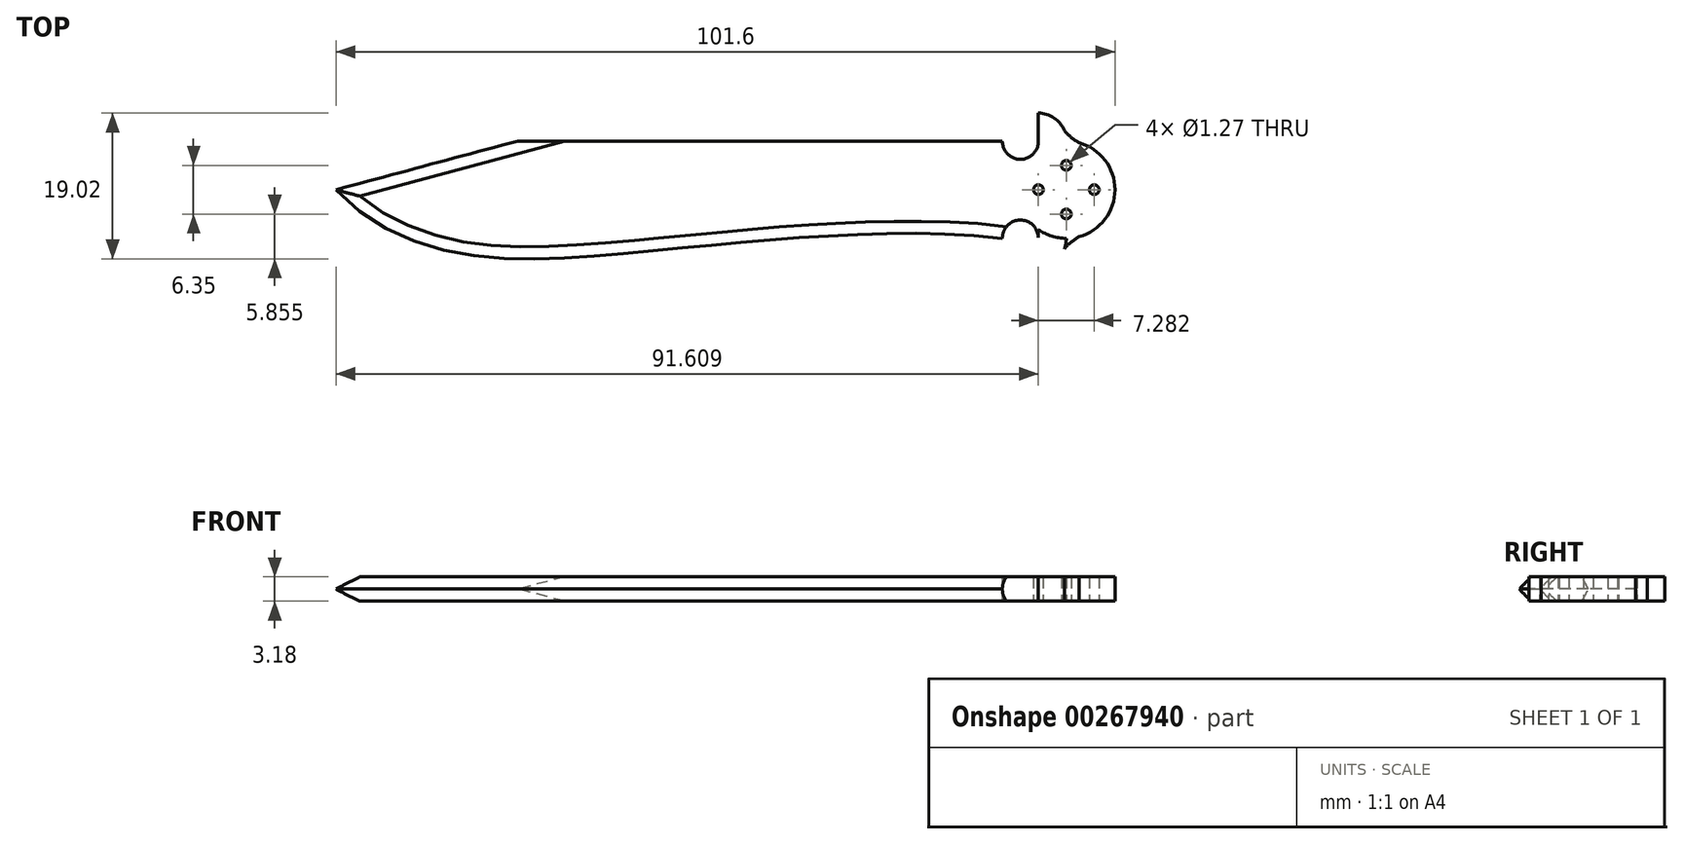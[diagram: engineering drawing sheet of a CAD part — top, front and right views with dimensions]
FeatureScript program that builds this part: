
annotation { "Feature Type Name" : "Feature", "Feature Type Description" : "" }
export const myFeature = defineFeature(function(context is Context, id is Id, definition is map)
    precondition{}
    {
        {
            var Q0;
            Q0=qCreatedBy(makeId("Top.planeOp"),FACE);
            var sketch = newSketch(context, id + "F0", { "sketchPlane" : qUnion([Q0])});
            skCircle(sketch, "E0", {"center": v(0, 0) * mm, "radius": 6.35 * mm});
            skLineSegment(sketch, "E1", {"start": v(0, -6.35) * mm, "end": v(0, 6.35) * mm});
            skArc(sketch, "E2", {"start": v(0, 6.35) * mm, "mid": v(-1.07, 8.92) * mm, "end": v(-3.64, 10) * mm});
            skLineSegment(sketch, "E3", {"start": v(-95.25, 0) * mm, "end": v(6.35, 0) * mm, "construction": true});
            skArc(sketch, "E4.MirrorCS", {"start": v(0, -6.35) * mm, "mid": v(-1.07, -8.92) * mm, "end": v(-3.64, -10) * mm});
            skLineSegment(sketch, "E5", {"start": v(-3.64, 10) * mm, "end": v(-3.64, 5.2) * mm});
            skLineSegment(sketch, "E6", {"start": v(-3.64, -10) * mm, "end": v(-3.64, -5.2) * mm});
            skArc(sketch, "E7", {"start": v(-8.34, 6.35) * mm, "mid": v(-5.99, 3.96) * mm, "end": v(-3.64, 6.35) * mm});
            skArc(sketch, "E8.MirrorCS", {"start": v(-8.34, -6.35) * mm, "mid": v(-5.99, -3.96) * mm, "end": v(-3.64, -6.35) * mm});
            skLineSegment(sketch, "E9", {"start": v(-95.25, 0) * mm, "end": v(-71.55, 6.35) * mm});
            skLineSegment(sketch, "E10", {"start": v(-8.34, 6.35) * mm, "end": v(-71.55, 6.35) * mm});
            skFitSpline(sketch, "E11", {"points": [v(-95.25, 0) * mm, v(-80.99, -7.93) * mm, v(-57.19, -8.28) * mm, v(-8.34, -6.35) * mm], "startDerivative": vector(42.5, -47.89) * mm, "endDerivative": vector(100.7, -12.48) * mm});
            skLineSegment(sketch, "E12", {"start": v(-95.25, 0) * mm, "end": v(-59.24, 6.35) * mm, "construction": true});
            skLineSegment(sketch, "E13", {"start": v(-3.64, 5.2) * mm, "end": v(-3.64, 0) * mm, "construction": true});
            skLineSegment(sketch, "E14", {"start": v(-3.64, 0) * mm, "end": v(-3.64, -5.2) * mm, "construction": true});
            skLineSegment(sketch, "E15.MirrorCS", {"start": v(3.64, 5.2) * mm, "end": v(3.64, 0) * mm, "construction": true});
            skLineSegment(sketch, "E16.MirrorCS", {"start": v(3.64, 0) * mm, "end": v(3.64, -5.2) * mm, "construction": true});
            skCircle(sketch, "E17", {"center": v(-3.64, 0) * mm, "radius": 0.64 * mm});
            skCircle(sketch, "E18", {"center": v(3.64, 0) * mm, "radius": 0.64 * mm});
            skLineSegment(sketch, "E19", {"start": v(0, 0) * mm, "end": v(0, 6.35) * mm, "construction": true});
            skLineSegment(sketch, "E20", {"start": v(0, 0) * mm, "end": v(0, -6.35) * mm, "construction": true});
            skCircle(sketch, "E21", {"center": v(0, -3.17) * mm, "radius": 0.64 * mm});
            skCircle(sketch, "E22", {"center": v(0, 3.17) * mm, "radius": 0.64 * mm});
            skFitSpline(sketch, "E23", {"points": [v(-1.07, 8.92) * mm, v(3.64, 5.2) * mm], "startDerivative": vector(3.04, -6.1) * mm, "endDerivative": vector(5.07, -1.86) * mm});
            skFitSpline(sketch, "E24.MirrorCS", {"points": [v(-1.07, -8.92) * mm, v(3.64, -5.2) * mm], "startDerivative": vector(3.04, 6.1) * mm, "endDerivative": vector(5.07, 1.86) * mm});
            skSolve(sketch);
        }
        {
            var Q0;
            {var subQ0=sQuery(id+"F0.wireOp",EDGE,"E9");Q0=makeQuery(id+"F0.imprint","IMPRINT",FACE,{"disambiguationData":[TD([[makeQuery(id+"F0.imprint","IMPRINT",EDGE,{"derivedFrom":subQ0}),-1.0]])]});}
            var Q1;
            Q1=makeQuery(id+"F0.imprint","IMPRINT",FACE,{"disambiguationData":[TD([[makeQuery(id+"F0.imprint","IMPRINT",EDGE,{"derivedFrom":sQuery(id+"F0.wireOp",EDGE,"E17")}),-1.0]])]});
            var Q2;
            Q2=makeQuery(id+"F0.imprint","IMPRINT",FACE,{"disambiguationData":[TD([[makeQuery(id+"F0.imprint","IMPRINT",EDGE,{"derivedFrom":sQuery(id+"F0.wireOp",EDGE,"E18")}),-1.0]])]});
            var Q3;
            {var subQ5=sQuery(id+"F0.wireOp",EDGE,"E2");Q3=makeQuery(id+"F0.imprint","IMPRINT",FACE,{"disambiguationData":[TD([[makeQuery(id+"F0.imprint","IMPRINT",EDGE,{"derivedFrom":subQ5}),1.0]])]});}
            var Q4;
            {var subQ5=sQuery(id+"F0.wireOp",EDGE,"E4.MirrorCS");Q4=makeQuery(id+"F0.imprint","IMPRINT",FACE,{"disambiguationData":[TD([[makeQuery(id+"F0.imprint","IMPRINT",EDGE,{"derivedFrom":subQ5}),-1.0]])]});}
            var Q5;
            {var subQ0=sQuery(id+"F0.wireOp",EDGE,"E23");var subQ1=sQuery(id+"F0.wireOp",EDGE,"E2");var subQ2=makeQuery(id+"F0.imprint","INTERSECT",VERTEX,{"disambiguationData":[OD(0.0)],"derivedFrom":[subQ1,subQ0]});Q5=makeQuery(id+"F0.imprint","IMPRINT",FACE,{"disambiguationData":[TD([[makeQuery(id+"F0.imprint","IMPRINT",EDGE,{"disambiguationData":[TD([[subQ2,1.0]])],"derivedFrom":subQ1}),1.0]])]});}
            var Q6;
            {var subQ1=sQuery(id+"F0.wireOp",EDGE,"E0");var subQ3=sQuery(id+"F0.wireOp",EDGE,"E23");var subQ4=makeQuery(id+"F0.imprint","INTERSECT",VERTEX,{"disambiguationData":[OD(1.0)],"derivedFrom":[subQ1,subQ3]});Q6=makeQuery(id+"F0.imprint","IMPRINT",FACE,{"disambiguationData":[TD([[makeQuery(id+"F0.imprint","IMPRINT",EDGE,{"disambiguationData":[TD([[subQ4,1.0]])],"derivedFrom":subQ3}),-1.0]])]});}
            var Q7;
            {var subQ0=sQuery(id+"F0.wireOp",EDGE,"E23");var subQ1=sQuery(id+"F0.wireOp",EDGE,"E0");var subQ2=makeQuery(id+"F0.imprint","INTERSECT",VERTEX,{"disambiguationData":[OD(0.0)],"derivedFrom":[subQ1,subQ0]});Q7=makeQuery(id+"F0.imprint","IMPRINT",FACE,{"disambiguationData":[TD([[makeQuery(id+"F0.imprint","IMPRINT",EDGE,{"disambiguationData":[TD([[subQ2,-1.0]])],"derivedFrom":subQ1}),1.0]])]});}
            var Q8;
            {var subQ1=sQuery(id+"F0.wireOp",EDGE,"E0");var subQ3=sQuery(id+"F0.wireOp",EDGE,"E24.MirrorCS");var subQ4=makeQuery(id+"F0.imprint","INTERSECT",VERTEX,{"disambiguationData":[OD(1.0)],"derivedFrom":[subQ1,subQ3]});Q8=makeQuery(id+"F0.imprint","IMPRINT",FACE,{"disambiguationData":[TD([[makeQuery(id+"F0.imprint","IMPRINT",EDGE,{"disambiguationData":[TD([[subQ4,1.0]])],"derivedFrom":subQ3}),1.0]])]});}
            var Q9;
            {var subQ0=sQuery(id+"F0.wireOp",EDGE,"E5");var subQ1=sQuery(id+"F0.wireOp",EDGE,"E0");var subQ2=makeQuery(id+"F0.imprint","INTERSECT",VERTEX,{"derivedFrom":[subQ1,subQ0]});Q9=makeQuery(id+"F0.imprint","IMPRINT",FACE,{"disambiguationData":[TD([[makeQuery(id+"F0.imprint","IMPRINT",EDGE,{"disambiguationData":[TD([[subQ2,-1.0]])],"derivedFrom":subQ1}),-1.0]])]});}
            var Q10;
            {var subQ0=sQuery(id+"F0.wireOp",EDGE,"E24.MirrorCS");var subQ1=sQuery(id+"F0.wireOp",EDGE,"E0");var subQ2=makeQuery(id+"F0.imprint","INTERSECT",VERTEX,{"disambiguationData":[OD(0.0)],"derivedFrom":[subQ1,subQ0]});Q10=makeQuery(id+"F0.imprint","IMPRINT",FACE,{"disambiguationData":[TD([[makeQuery(id+"F0.imprint","IMPRINT",EDGE,{"disambiguationData":[TD([[subQ2,1.0]])],"derivedFrom":subQ1}),1.0]])]});}
            var Q11;
            {var subQ0=sQuery(id+"F0.wireOp",EDGE,"E24.MirrorCS");var subQ1=sQuery(id+"F0.wireOp",EDGE,"E4.MirrorCS");var subQ2=makeQuery(id+"F0.imprint","INTERSECT",VERTEX,{"disambiguationData":[OD(0.0)],"derivedFrom":[subQ1,subQ0]});Q11=makeQuery(id+"F0.imprint","IMPRINT",FACE,{"disambiguationData":[TD([[makeQuery(id+"F0.imprint","IMPRINT",EDGE,{"disambiguationData":[TD([[subQ2,1.0]])],"derivedFrom":subQ1}),-1.0]])]});}
            var Q12;
            {var subQ0=sQuery(id+"F0.wireOp",EDGE,"E6");var subQ1=sQuery(id+"F0.wireOp",EDGE,"E0");var subQ2=makeQuery(id+"F0.imprint","INTERSECT",VERTEX,{"derivedFrom":[subQ1,subQ0]});Q12=makeQuery(id+"F0.imprint","IMPRINT",FACE,{"disambiguationData":[TD([[makeQuery(id+"F0.imprint","IMPRINT",EDGE,{"disambiguationData":[TD([[subQ2,1.0]])],"derivedFrom":subQ1}),-1.0]])]});}
            extrude(context, id + "F1", {"entities" : qUnion([Q0, Q1, Q2, Q3, Q4, Q5, Q6, Q7, Q8, Q9, Q10, Q11, Q12]), "depth" : 3.17 * mm, "offsetDistance" : 25.4 * mm});
        }
        {
            var Q0;
            Q0=makeQuery(id+"F1.opExtrude","CAP_EDGE",EDGE,{"disambiguationData":[OSD([sQuery(id+"F0.wireOp",EDGE,"E11")])],"isStart":true});
            var Q1;
            Q1=makeQuery(id+"F1.opExtrude","CAP_EDGE",EDGE,{"disambiguationData":[OSD([sQuery(id+"F0.wireOp",EDGE,"E11")])],"isStart":false});
            var Q2;
            Q2=makeQuery(id+"F1.opExtrude","CAP_EDGE",EDGE,{"disambiguationData":[OSD([sQuery(id+"F0.wireOp",EDGE,"E9")])],"isStart":true});
            var Q3;
            Q3=makeQuery(id+"F1.opExtrude","CAP_EDGE",EDGE,{"disambiguationData":[OSD([sQuery(id+"F0.wireOp",EDGE,"E9")])],"isStart":false});
            chamfer(context, id + "F2", {"entities" : qUnion([Q0, Q1, Q2, Q3]), "width" : 1.59 * mm, "tangentPropagation" : true});
        }
    });
